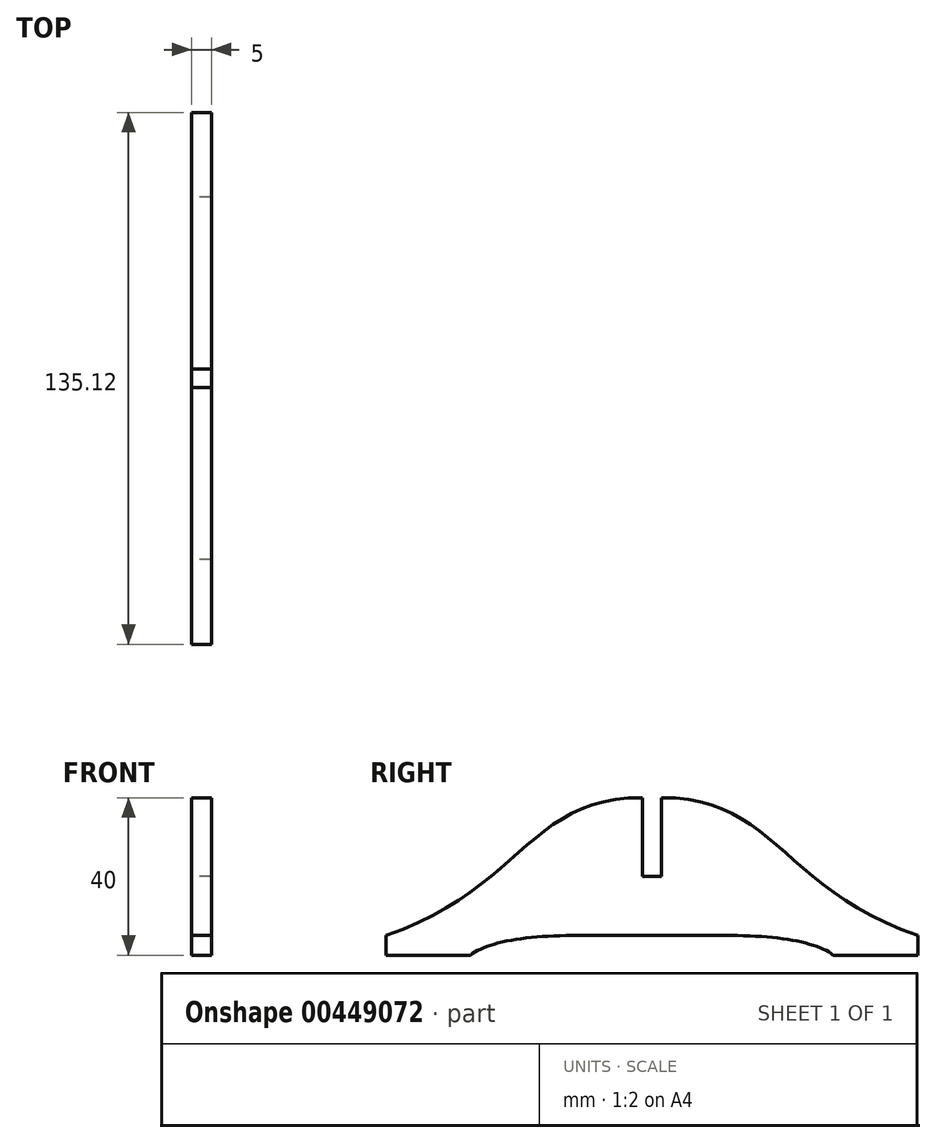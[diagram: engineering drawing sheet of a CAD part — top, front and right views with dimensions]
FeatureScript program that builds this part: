
annotation { "Feature Type Name" : "Feature", "Feature Type Description" : "" }
export const myFeature = defineFeature(function(context is Context, id is Id, definition is map)
    precondition{}
    {
        {
            var Q0;
            Q0=qCreatedBy(makeId("Right.planeOp"),FACE);
            var sketch = newSketch(context, id + "F0", { "sketchPlane" : qUnion([Q0])});
            skLineSegment(sketch, "E0.bottom", {"start": v(0, 0) * mm, "end": v(2.4, 0) * mm});
            skLineSegment(sketch, "E0.top", {"start": v(0, 40) * mm, "end": v(2.4, 40) * mm});
            skLineSegment(sketch, "E0.left", {"start": v(0, 0) * mm, "end": v(0, 40) * mm});
            skLineSegment(sketch, "E0.right", {"start": v(2.4, 0) * mm, "end": v(2.4, 40) * mm});
            skLineSegment(sketch, "E1", {"start": v(2.4, 0) * mm, "end": v(67.56, 0) * mm});
            skLineSegment(sketch, "E2", {"start": v(67.56, 0) * mm, "end": v(67.56, 5) * mm});
            skFitSpline(sketch, "E3", {"points": [v(2.4, 40) * mm, v(67.56, 5) * mm], "startDerivative": vector(85.2, 1) * mm, "endDerivative": vector(102.74, -35.11) * mm});
            skLineSegment(sketch, "E4.bottom", {"start": v(2.4, 0) * mm, "end": v(0, 0) * mm});
            skLineSegment(sketch, "E4.top", {"start": v(2.4, 20) * mm, "end": v(0, 20) * mm});
            skLineSegment(sketch, "E4.left", {"start": v(2.4, 0) * mm, "end": v(2.4, 20) * mm});
            skLineSegment(sketch, "E4.right", {"start": v(0, 0) * mm, "end": v(0, 20) * mm});
            skLineSegment(sketch, "E5.MirrorCS", {"start": v(0, 0) * mm, "end": v(-2.4, 0) * mm});
            skLineSegment(sketch, "E6.MirrorCS", {"start": v(-2.4, 0) * mm, "end": v(0, 0) * mm});
            skLineSegment(sketch, "E7.MirrorCS", {"start": v(0, 40) * mm, "end": v(-2.4, 40) * mm});
            skLineSegment(sketch, "E8.MirrorCS", {"start": v(-2.4, 20) * mm, "end": v(0, 20) * mm});
            skLineSegment(sketch, "E9.MirrorCS", {"start": v(-2.4, 0) * mm, "end": v(-2.4, 20) * mm});
            skLineSegment(sketch, "E10.MirrorCS", {"start": v(-2.4, 0) * mm, "end": v(-67.56, 0) * mm});
            skLineSegment(sketch, "E11.MirrorCS", {"start": v(-67.56, 0) * mm, "end": v(-67.56, 5) * mm});
            skLineSegment(sketch, "E12.MirrorCS", {"start": v(-2.4, 0) * mm, "end": v(-2.4, 40) * mm});
            skFitSpline(sketch, "E13.MirrorCS", {"points": [v(-2.4, 40) * mm, v(-67.56, 5) * mm], "startDerivative": vector(-85.2, 1) * mm, "endDerivative": vector(-102.74, -35.11) * mm});
            skLineSegment(sketch, "E14", {"start": v(2.4, 5) * mm, "end": v(20.19, 5) * mm});
            skFitSpline(sketch, "E15", {"points": [v(46.06, 0) * mm, v(20.19, 5) * mm], "startDerivative": vector(-11.3, 9.5) * mm, "endDerivative": vector(-36.8, 0) * mm});
            skFitSpline(sketch, "E16.MirrorCS", {"points": [v(-46.06, 0) * mm, v(-20.19, 5) * mm], "startDerivative": vector(11.3, 9.5) * mm, "endDerivative": vector(36.8, 0) * mm});
            skLineSegment(sketch, "E17.MirrorCS", {"start": v(-2.4, 5) * mm, "end": v(-20.19, 5) * mm});
            skLineSegment(sketch, "E18", {"start": v(-2.4, 5) * mm, "end": v(2.4, 5) * mm});
            skSolve(sketch);
        }
        {
            var Q0;
            Q0=makeQuery(id+"F0.imprint","IMPRINT",FACE,{"disambiguationData":[TD([[makeQuery(id+"F0.imprint","IMPRINT",EDGE,{"derivedFrom":sQuery(id+"F0.wireOp",EDGE,"E0.right")}),-1.0]])]});
            var Q1;
            {var subQ0=sQuery(id+"F0.wireOp",EDGE,"E4.top");Q1=makeQuery(id+"F0.imprint","IMPRINT",FACE,{"disambiguationData":[TD([[makeQuery(id+"F0.imprint","IMPRINT",EDGE,{"derivedFrom":subQ0}),1.0]])]});}
            var Q2;
            {var subQ0=sQuery(id+"F0.wireOp",EDGE,"E8.MirrorCS");Q2=makeQuery(id+"F0.imprint","IMPRINT",FACE,{"disambiguationData":[TD([[makeQuery(id+"F0.imprint","IMPRINT",EDGE,{"derivedFrom":subQ0}),-1.0]])]});}
            var Q3;
            {var subQ4=sQuery(id+"F0.wireOp",EDGE,"E11.MirrorCS");Q3=makeQuery(id+"F0.imprint","IMPRINT",FACE,{"disambiguationData":[TD([[makeQuery(id+"F0.imprint","IMPRINT",EDGE,{"derivedFrom":subQ4}),-1.0]])]});}
            extrude(context, id + "F1", {"entities" : qUnion([Q0, Q1, Q2, Q3]), "depth" : 5 * mm});
        }
    });
